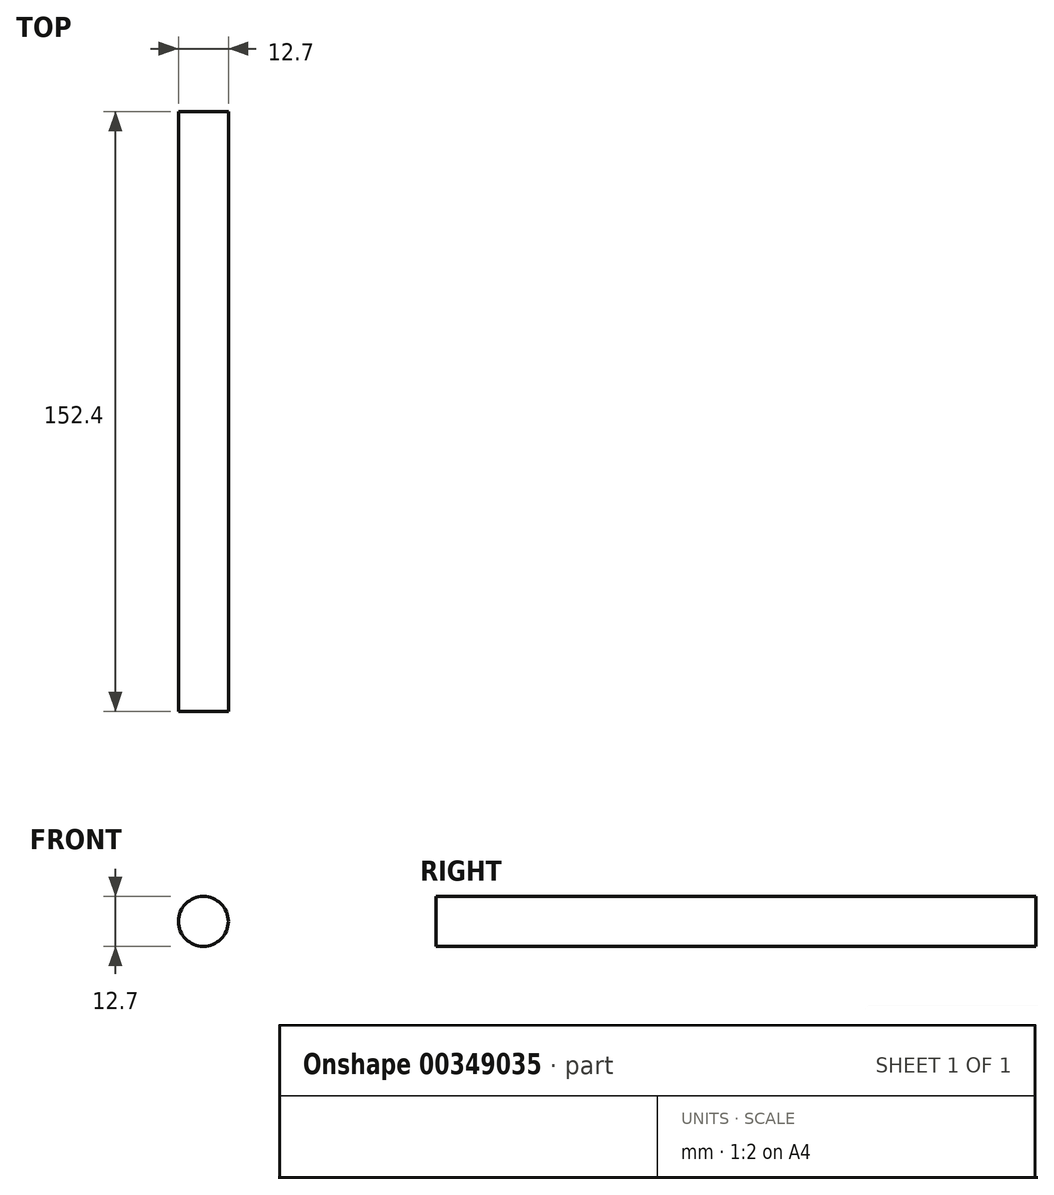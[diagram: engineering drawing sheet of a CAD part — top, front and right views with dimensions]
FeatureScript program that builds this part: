
annotation { "Feature Type Name" : "Feature", "Feature Type Description" : "" }
export const myFeature = defineFeature(function(context is Context, id is Id, definition is map)
    precondition{}
    {
        {
            var Q0;
            Q0=qCreatedBy(makeId("Front.planeOp"),FACE);
            var sketch = newSketch(context, id + "F0", { "sketchPlane" : qUnion([Q0])});
            skCircle(sketch, "E0", {"center": v(0, 0) * mm, "radius": 6.35 * mm});
            skSolve(sketch);
        }
        {
            var Q0;
            Q0=makeQuery(id+"F0.imprint","IMPRINT",FACE,{"disambiguationData":[TD([[makeQuery(id+"F0.imprint","IMPRINT",EDGE,{"derivedFrom":sQuery(id+"F0.wireOp",EDGE,"E0")}),1.0]])]});
            extrude(context, id + "F1", {"entities" : qUnion([Q0]), "endBound" : BoundingType.SYMMETRIC, "depth" : 152.4 * mm});
        }
    });
